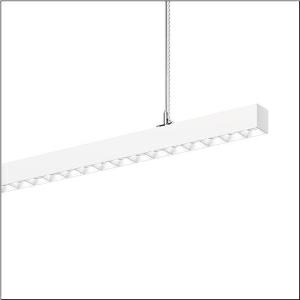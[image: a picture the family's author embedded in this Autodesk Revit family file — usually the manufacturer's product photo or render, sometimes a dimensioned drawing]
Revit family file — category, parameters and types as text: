
# Revit family: silica_r__21_51mx36da37wb_45fb
name_source: partatom
category: Lighting Fixtures
units: mm (PartAtom-declared; Revit-internal decimal feet)

## family parameters
Cut with Voids When Loaded = No
Host = Face
Light Source = No
Part Type = Normal
Room Calculation Point = No
Round Connector Dimension = Use Diameter
Shared = No

## types (1)
- --- (1 x LED, 7060 lm, 43 W, 3000K)
    Apparent Load = 43 VA
    CIE Flux Codes = 83 98 100 61 100
    Color Rendering = 80
    Color Temperature = 3000K
    Default Elevation = 1800 mm
    Description = Silica® 21, office luminaire, primary light control with darklight reflector, of PMMA, white, CAT 2 (L<= 3000cd/m²), light emission: direct/indirect distribution, primary light characteristic: symmetric, installation type: suspended mounting, LED, rated luminous flux: 7.060lm, luminous efficacy: 164lm/W, light colour: 830, colour temperature: 3000K, with terminal, 3+2-pole, max. 2.5mm², mains connection: 220..240V, AC, 50/60Hz, rated input power: 43W, luminaire housing, of aluminium, traffic white (RAL 9016), length: 1.204mm, width: 53mm, height: 53mm, protection rating (complete): IP20, insulation class (complete): insulation class I (protective earthing), certification: CE, permissible operating ambient temperature: 0..+35°C, standard: EN 50419, packaging unit: 1 piece
    Height = 53 mm
    Lamp = 1 x LED
    Lamp Light Flux = 7060 lm
    Lamp Power = 43 W
    Lamp count = 1
    Length = 1204 mm
    Luminous efficacy = 164 lm/W
    Manufacturer = Siteco
    ModVariant = No
    Model = 51MX36DA37WB
    Mounting Place = Ceiling
    Mounting Type = Pendant
    Number of Poles = 1
    OnlyDefault = Yes
    Power Factor = 1
    Product Name = Silica® 21
    Product group = office luminaire | ceiling pendant
    ProductGroupID = 902
    Protection Class = Protection class I
    Protection Degree = IP 20
    RLX_Detail_Level = 1
    RLX_Emergency_Light_Flux = 0 lm
    RLX_Emergency_Type = 0
    RLX_Emergency_Type_DB = No
    RlxData = <blob elided: 40837 chars, md5=b2ed1761>
    Socket = socket
    Standby Power = 0 W
    System Light Flux = 7060 lm
    System Power = 43 W
    Type Comments = factory setting: luminous flux: 100 % | dim-lin: 254 | 359 mA
    Type Image = l_1335921.jpg
    URL = http://relux.com
    VarID = @adj_090857
    Voltage = 0 V
    Weight = 0.00 kg
    Width = 53 mm

## geometry (parser evidence)
native form markers: Blend x4, Sweep x13
no freeform markers — native parametric forms only
